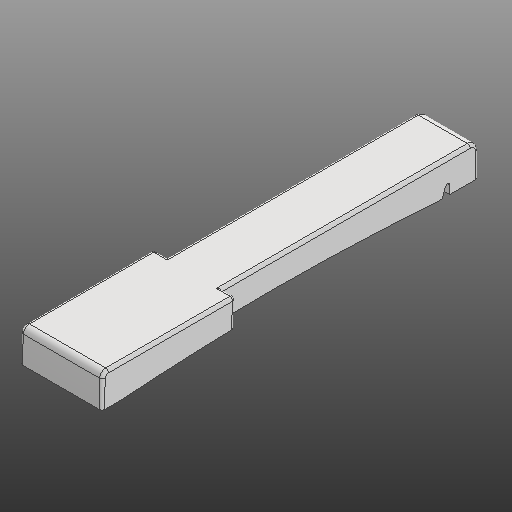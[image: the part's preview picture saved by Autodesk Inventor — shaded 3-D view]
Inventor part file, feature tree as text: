
AUTODESK INVENTOR PART (.ipt)
format: ipt  version: 2020 (Build 240168000, 168)  size: 313,856 bytes
history: native  units: in
note: dims shown in document units (in); Inventor stores cm internally (conversion verified against a paired STEP export)
features: extrude x4, other x3, fillet x2
ambient origin geometry x8: Origin, YZ Plane, XZ Plane, XY Plane, X Axis, Y Axis, Z Axis, Center Point
bodies: Solid1 (feature_tree)
feature tree (9):
  other  "Slot Start Plane"
  other  "Key Profile"
  extrude  "Upper"  TaperAngle=0.0deg  [1 undecoded]
  extrude  "Lower"  TaperAngle=0.0deg  [1 undecoded]
  extrude  "Protrusion Cutout"  Depth=0.0591in
  fillet  "Front Fillet"  Radius=0.1374in
  extrude  "Slot"  [1 undecoded]
  fillet  "Edge Softening"  Radius=0.0787in
  other  "Slot Sketch"
note: 3 required parameter values undecoded (feature->parameter linkage not recoverable at this tier; creation-order binding heuristic only, values carry confidence <= 0.55)
